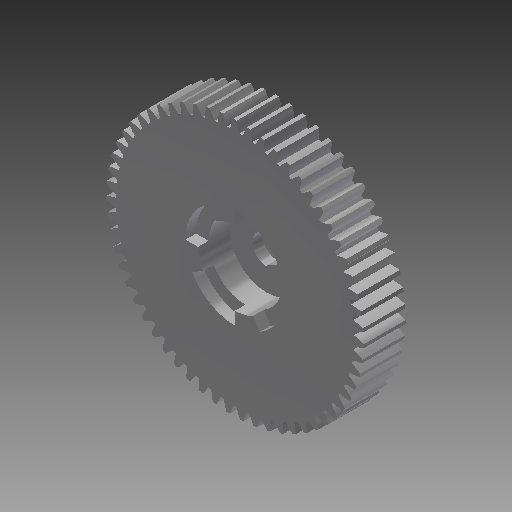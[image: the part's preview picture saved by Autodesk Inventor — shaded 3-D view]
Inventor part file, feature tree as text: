
AUTODESK INVENTOR PART (.ipt)
format: ipt  version: 2017 (Build 210142000, 142)  size: 433,664 bytes
history: native  units: mm (DEFAULTED — no unit token found)
features: sketch x5, extrude x4, plane x3, other x3, pattern_circular x1
ambient origin geometry x8: Origin, YZ Plane, XZ Plane, XY Plane, X Axis, Y Axis, Z Axis, Center Point
bodies: Solid1 (feature_tree)
feature tree (16):
  extrude  "Extrusion1"  Depth=20.0mm TaperAngle=0.0deg
  plane  "Work Plane2"
  plane  "Work Plane8"
  plane  "Work Plane9"
  other  "Spur Gear"
  extrude  "Extrusion2"  Depth=10.0mm TaperAngle=0.0deg
  extrude  "Extrusion3"  Depth=0.532473mm TaperAngle=0.0deg
  extrude  "Extrusion4"  TaperAngle=0.0deg  [1 undecoded]
  pattern_circular  "Circular Pattern1"  Count=8  [1 undecoded]
  sketch  "Sketch1"  dims[d0=122.0mm d1=20.0mm d2=0.0mm]
  sketch  "Sketch2"  dims[d3=118.0mm d4=10.0mm d5=0.0mm]
  other  "Srf1"
  sketch  "Sketch3"  dims[d16=80.0mm d17=0.0mm d34=0.532473mm]
  sketch  "Sketch4"  dims[d39=0.0mm d41=0.0mm d43=80.0mm]
  sketch  "Sketch5"  dims[d46=80.0mm d47=0.0mm d48=0.0mm d49=13.5mm d50=10.0mm d51=0.0mm d52=35.0mm d53=15.0mm d54=0.0mm d55=60.0deg d56=6.0mm d57=5.0mm d58=0.0mm d59=40.0mm d60=360.0deg]
  other  "Pitch Diameter"
note: 2 required parameter values undecoded (feature->parameter linkage not recoverable at this tier; creation-order binding heuristic only, values carry confidence <= 0.55)
